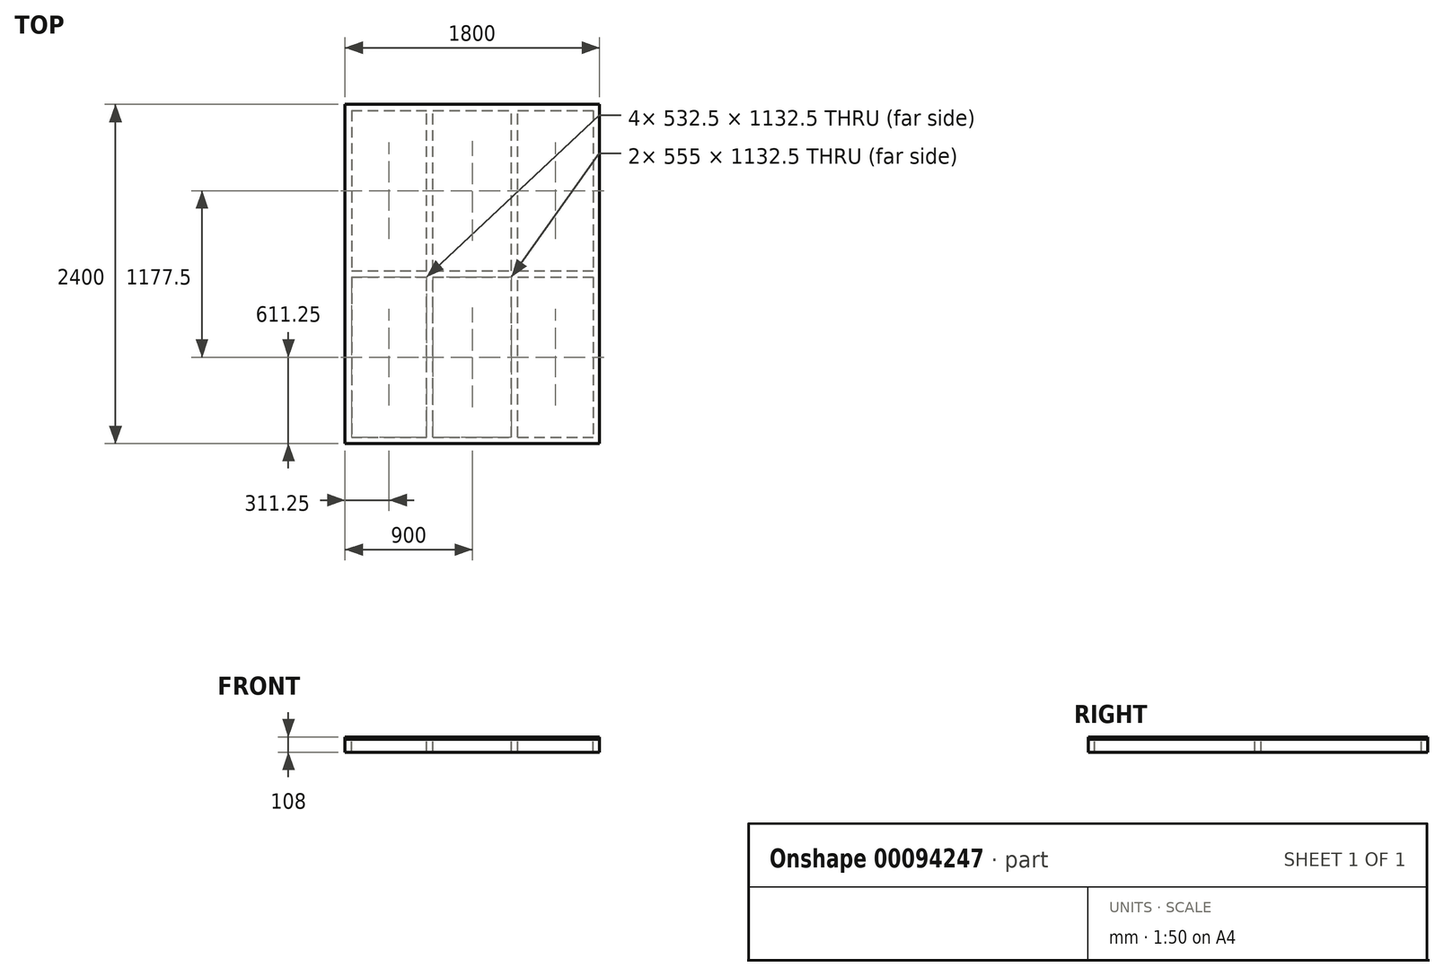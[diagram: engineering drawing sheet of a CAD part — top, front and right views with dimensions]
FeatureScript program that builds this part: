
annotation { "Feature Type Name" : "Feature", "Feature Type Description" : "" }
export const myFeature = defineFeature(function(context is Context, id is Id, definition is map)
    precondition{}
    {
        {
            var Q0;
            Q0=qCreatedBy(makeId("Top.planeOp"),FACE);
            var sketch = newSketch(context, id + "F0", { "sketchPlane" : qUnion([Q0])});
            skLineSegment(sketch, "E0.bottom", {"start": v(900, -1200) * mm, "end": v(-900, -1200) * mm});
            skLineSegment(sketch, "E0.top", {"start": v(900, 1200) * mm, "end": v(-900, 1200) * mm});
            skLineSegment(sketch, "E0.left", {"start": v(900, -1200) * mm, "end": v(900, 1200) * mm});
            skLineSegment(sketch, "E0.right", {"start": v(-900, -1200) * mm, "end": v(-900, 1200) * mm});
            skLineSegment(sketch, "E1", {"start": v(-900, -1155) * mm, "end": v(900, -1155) * mm});
            skLineSegment(sketch, "E2", {"start": v(-900, 1155) * mm, "end": v(900, 1155) * mm});
            skLineSegment(sketch, "E3", {"start": v(-855, 1155) * mm, "end": v(-855, -1155) * mm});
            skLineSegment(sketch, "E4", {"start": v(0, 1459.19) * mm, "end": v(0, -1485.9) * mm, "construction": true});
            skPoint(sketch, "E4.endSnap0", {"position": v(0, -1200) * mm});
            skLineSegment(sketch, "E5.MirrorCS", {"start": v(855, 1155) * mm, "end": v(855, -1155) * mm});
            skLineSegment(sketch, "E6", {"start": v(-322.5, -1155) * mm, "end": v(-322.5, 1155) * mm});
            skLineSegment(sketch, "E7", {"start": v(-300, -1155) * mm, "end": v(-300, 1155) * mm, "construction": true});
            skLineSegment(sketch, "E8.MirrorCS", {"start": v(-277.5, -1155) * mm, "end": v(-277.5, 1155) * mm});
            skLineSegment(sketch, "E9.MirrorCS", {"start": v(277.5, -1155) * mm, "end": v(277.5, 1155) * mm});
            skLineSegment(sketch, "E10.MirrorCS", {"start": v(322.5, -1155) * mm, "end": v(322.5, 1155) * mm});
            skLineSegment(sketch, "E11", {"start": v(-855, 0) * mm, "end": v(855, 0) * mm, "construction": true});
            skLineSegment(sketch, "E12", {"start": v(-855, 22.5) * mm, "end": v(-322.5, 22.5) * mm});
            skLineSegment(sketch, "E13.MirrorCS", {"start": v(-855, -22.5) * mm, "end": v(-322.5, -22.5) * mm});
            skLineSegment(sketch, "E14.trimOffspring", {"start": v(-277.5, -22.5) * mm, "end": v(277.5, -22.5) * mm});
            skLineSegment(sketch, "E15.trimOffspring", {"start": v(-277.5, 22.5) * mm, "end": v(277.5, 22.5) * mm});
            skLineSegment(sketch, "E16.trimOffspring", {"start": v(322.5, -22.5) * mm, "end": v(855, -22.5) * mm});
            skLineSegment(sketch, "E17.trimOffspring", {"start": v(322.5, 22.5) * mm, "end": v(855, 22.5) * mm});
            skSolve(sketch);
        }
        {
            var Q0;
            {var subQ0=sQuery(id+"F0.wireOp",EDGE,"E9.MirrorCS");var subQ3=sQuery(id+"F0.wireOp",EDGE,"E1");var subQ4=makeQuery(id+"F0.imprint","INTERSECT",VERTEX,{"derivedFrom":[subQ3,subQ0]});Q0=makeQuery(id+"F0.imprint","IMPRINT",FACE,{"disambiguationData":[TD([[makeQuery(id+"F0.imprint","IMPRINT",EDGE,{"disambiguationData":[TD([[subQ4,-1.0]])],"derivedFrom":subQ3}),1.0]])]});}
            var Q1;
            {var subQ0=sQuery(id+"F0.wireOp",EDGE,"E16.trimOffspring");Q1=makeQuery(id+"F0.imprint","IMPRINT",FACE,{"disambiguationData":[TD([[makeQuery(id+"F0.imprint","IMPRINT",EDGE,{"derivedFrom":subQ0}),1.0]])]});}
            var Q2;
            {var subQ0=sQuery(id+"F0.wireOp",EDGE,"E14.trimOffspring");Q2=makeQuery(id+"F0.imprint","IMPRINT",FACE,{"disambiguationData":[TD([[makeQuery(id+"F0.imprint","IMPRINT",EDGE,{"derivedFrom":subQ0}),1.0]])]});}
            var Q3;
            {var subQ0=sQuery(id+"F0.wireOp",EDGE,"E12");Q3=makeQuery(id+"F0.imprint","IMPRINT",FACE,{"disambiguationData":[TD([[makeQuery(id+"F0.imprint","IMPRINT",EDGE,{"derivedFrom":subQ0}),-1.0]])]});}
            var Q4;
            {var subQ0=sQuery(id+"F0.wireOp",EDGE,"E6");var subQ7=sQuery(id+"F0.wireOp",EDGE,"E1");var subQ8=makeQuery(id+"F0.imprint","INTERSECT",VERTEX,{"derivedFrom":[subQ7,subQ0]});Q4=makeQuery(id+"F0.imprint","IMPRINT",FACE,{"disambiguationData":[TD([[makeQuery(id+"F0.imprint","IMPRINT",EDGE,{"disambiguationData":[TD([[subQ8,-1.0]])],"derivedFrom":subQ7}),1.0]])]});}
            var Q5;
            {var subQ1=sQuery(id+"F0.wireOp",EDGE,"E0.right");var subQ5=sQuery(id+"F0.wireOp",EDGE,"E1");var subQ6=makeQuery(id+"F0.imprint","INTERSECT",VERTEX,{"derivedFrom":[subQ1,subQ5]});Q5=makeQuery(id+"F0.imprint","IMPRINT",FACE,{"disambiguationData":[TD([[makeQuery(id+"F0.imprint","IMPRINT",EDGE,{"disambiguationData":[TD([[subQ6,-1.0]])],"derivedFrom":subQ1}),-1.0]])]});}
            var Q6;
            {var subQ4=sQuery(id+"F0.wireOp",EDGE,"E1");var subQ5=sQuery(id+"F0.wireOp",EDGE,"E0.left");var subQ6=makeQuery(id+"F0.imprint","INTERSECT",VERTEX,{"derivedFrom":[subQ5,subQ4]});Q6=makeQuery(id+"F0.imprint","IMPRINT",FACE,{"disambiguationData":[TD([[makeQuery(id+"F0.imprint","IMPRINT",EDGE,{"disambiguationData":[TD([[subQ6,-1.0]])],"derivedFrom":subQ5}),1.0]])]});}
            var Q7;
            {var subQ4=sQuery(id+"F0.wireOp",EDGE,"E0.bottom");Q7=makeQuery(id+"F0.imprint","IMPRINT",FACE,{"disambiguationData":[TD([[makeQuery(id+"F0.imprint","IMPRINT",EDGE,{"derivedFrom":subQ4}),-1.0]])]});}
            var Q8;
            {var subQ4=sQuery(id+"F0.wireOp",EDGE,"E0.top");Q8=makeQuery(id+"F0.imprint","IMPRINT",FACE,{"disambiguationData":[TD([[makeQuery(id+"F0.imprint","IMPRINT",EDGE,{"derivedFrom":subQ4}),1.0]])]});}
            extrude(context, id + "F1", {"entities" : qUnion([Q0, Q1, Q2, Q3, Q4, Q5, Q6, Q7, Q8]), "oppositeDirection" : true, "depth" : 90 * mm});
        }
        {
            var Q0;
            {var subQ5=sQuery(id+"F0.wireOp",EDGE,"E17.trimOffspring");Q0=makeQuery(id+"F0.imprint","IMPRINT",FACE,{"disambiguationData":[TD([[makeQuery(id+"F0.imprint","IMPRINT",EDGE,{"derivedFrom":subQ5}),1.0]])]});}
            var Q1;
            {var subQ5=sQuery(id+"F0.wireOp",EDGE,"E16.trimOffspring");Q1=makeQuery(id+"F0.imprint","IMPRINT",FACE,{"disambiguationData":[TD([[makeQuery(id+"F0.imprint","IMPRINT",EDGE,{"derivedFrom":subQ5}),-1.0]])]});}
            var Q2;
            {var subQ5=sQuery(id+"F0.wireOp",EDGE,"E13.MirrorCS");Q2=makeQuery(id+"F0.imprint","IMPRINT",FACE,{"disambiguationData":[TD([[makeQuery(id+"F0.imprint","IMPRINT",EDGE,{"derivedFrom":subQ5}),-1.0]])]});}
            var Q3;
            {var subQ0=sQuery(id+"F0.wireOp",EDGE,"E12");Q3=makeQuery(id+"F0.imprint","IMPRINT",FACE,{"disambiguationData":[TD([[makeQuery(id+"F0.imprint","IMPRINT",EDGE,{"derivedFrom":subQ0}),-1.0]])]});}
            var Q4;
            {var subQ0=sQuery(id+"F0.wireOp",EDGE,"E16.trimOffspring");Q4=makeQuery(id+"F0.imprint","IMPRINT",FACE,{"disambiguationData":[TD([[makeQuery(id+"F0.imprint","IMPRINT",EDGE,{"derivedFrom":subQ0}),1.0]])]});}
            var Q5;
            {var subQ4=sQuery(id+"F0.wireOp",EDGE,"E1");var subQ5=sQuery(id+"F0.wireOp",EDGE,"E0.left");var subQ6=makeQuery(id+"F0.imprint","INTERSECT",VERTEX,{"derivedFrom":[subQ5,subQ4]});Q5=makeQuery(id+"F0.imprint","IMPRINT",FACE,{"disambiguationData":[TD([[makeQuery(id+"F0.imprint","IMPRINT",EDGE,{"disambiguationData":[TD([[subQ6,-1.0]])],"derivedFrom":subQ5}),1.0]])]});}
            var Q6;
            {var subQ4=sQuery(id+"F0.wireOp",EDGE,"E0.top");Q6=makeQuery(id+"F0.imprint","IMPRINT",FACE,{"disambiguationData":[TD([[makeQuery(id+"F0.imprint","IMPRINT",EDGE,{"derivedFrom":subQ4}),1.0]])]});}
            var Q7;
            {var subQ1=sQuery(id+"F0.wireOp",EDGE,"E0.right");var subQ5=sQuery(id+"F0.wireOp",EDGE,"E1");var subQ6=makeQuery(id+"F0.imprint","INTERSECT",VERTEX,{"derivedFrom":[subQ1,subQ5]});Q7=makeQuery(id+"F0.imprint","IMPRINT",FACE,{"disambiguationData":[TD([[makeQuery(id+"F0.imprint","IMPRINT",EDGE,{"disambiguationData":[TD([[subQ6,-1.0]])],"derivedFrom":subQ1}),-1.0]])]});}
            var Q8;
            {var subQ4=sQuery(id+"F0.wireOp",EDGE,"E0.bottom");Q8=makeQuery(id+"F0.imprint","IMPRINT",FACE,{"disambiguationData":[TD([[makeQuery(id+"F0.imprint","IMPRINT",EDGE,{"derivedFrom":subQ4}),-1.0]])]});}
            var Q9;
            {var subQ5=sQuery(id+"F0.wireOp",EDGE,"E14.trimOffspring");Q9=makeQuery(id+"F0.imprint","IMPRINT",FACE,{"disambiguationData":[TD([[makeQuery(id+"F0.imprint","IMPRINT",EDGE,{"derivedFrom":subQ5}),-1.0]])]});}
            var Q10;
            {var subQ5=sQuery(id+"F0.wireOp",EDGE,"E15.trimOffspring");Q10=makeQuery(id+"F0.imprint","IMPRINT",FACE,{"disambiguationData":[TD([[makeQuery(id+"F0.imprint","IMPRINT",EDGE,{"derivedFrom":subQ5}),1.0]])]});}
            var Q11;
            {var subQ5=sQuery(id+"F0.wireOp",EDGE,"E12");Q11=makeQuery(id+"F0.imprint","IMPRINT",FACE,{"disambiguationData":[TD([[makeQuery(id+"F0.imprint","IMPRINT",EDGE,{"derivedFrom":subQ5}),1.0]])]});}
            var Q12;
            {var subQ0=sQuery(id+"F0.wireOp",EDGE,"E14.trimOffspring");Q12=makeQuery(id+"F0.imprint","IMPRINT",FACE,{"disambiguationData":[TD([[makeQuery(id+"F0.imprint","IMPRINT",EDGE,{"derivedFrom":subQ0}),1.0]])]});}
            var Q13;
            {var subQ0=sQuery(id+"F0.wireOp",EDGE,"E6");var subQ7=sQuery(id+"F0.wireOp",EDGE,"E1");var subQ8=makeQuery(id+"F0.imprint","INTERSECT",VERTEX,{"derivedFrom":[subQ7,subQ0]});Q13=makeQuery(id+"F0.imprint","IMPRINT",FACE,{"disambiguationData":[TD([[makeQuery(id+"F0.imprint","IMPRINT",EDGE,{"disambiguationData":[TD([[subQ8,-1.0]])],"derivedFrom":subQ7}),1.0]])]});}
            var Q14;
            {var subQ0=sQuery(id+"F0.wireOp",EDGE,"E9.MirrorCS");var subQ3=sQuery(id+"F0.wireOp",EDGE,"E1");var subQ4=makeQuery(id+"F0.imprint","INTERSECT",VERTEX,{"derivedFrom":[subQ3,subQ0]});Q14=makeQuery(id+"F0.imprint","IMPRINT",FACE,{"disambiguationData":[TD([[makeQuery(id+"F0.imprint","IMPRINT",EDGE,{"disambiguationData":[TD([[subQ4,-1.0]])],"derivedFrom":subQ3}),1.0]])]});}
            extrude(context, id + "F2", {"entities" : qUnion([Q0, Q1, Q2, Q3, Q4, Q5, Q6, Q7, Q8, Q9, Q10, Q11, Q12, Q13, Q14]), "depth" : 18 * mm});
        }
    });
